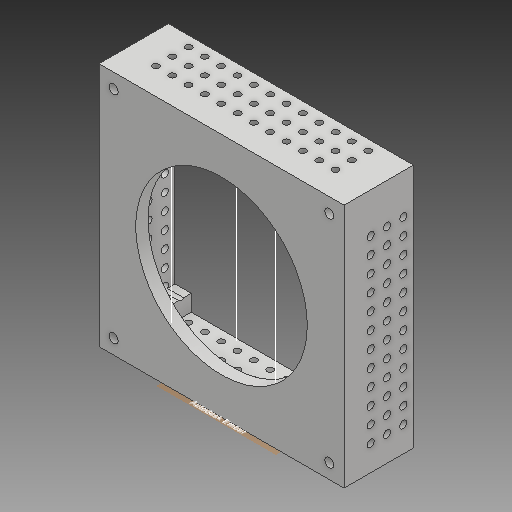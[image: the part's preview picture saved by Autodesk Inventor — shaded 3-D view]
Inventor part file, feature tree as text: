
AUTODESK INVENTOR PART (.ipt)
format: ipt  version: 2018 (Build 220112000, 112)  size: 508,416 bytes
history: native  units: mm
features: sketch x8, extrude x5, pattern_linear x2
ambient origin geometry x8: Origin, YZ Plane, XZ Plane, XY Plane, X Axis, Y Axis, Z Axis, Center Point
bodies: Solid1 (feature_tree)
feature tree (15):
  sketch  "Sketch1"  dims[d0=150.0mm d1=150.0mm]
  extrude  "Extrusion1"  Depth=150.0mm
  extrude  "Extrusion3"  Depth=4.0mm
  extrude  "Extrusion4"  Depth=10.0mm
  pattern_linear  "Rectangular Pattern1"  Count1=2 Spacing1=132.0mm
  extrude  "Extrusion5"  Depth=132.0mm
  pattern_linear  "Rectangular Pattern2"  Count1=8 Spacing1=0.0mm
  sketch  "Sketch9"  dims[d17=20.0mm d19=132.0mm d20=5.5mm d21=80.0mm d22=0.0mm]
  extrude  "Extrusion8"  Depth=132.0mm
  sketch  "Sketch11"  dims[d45=4.0mm d46=40.0mm d47=0.0mm]
  sketch  "Sketch2"  dims[d2=7.5mm d3=0.0mm d7=4.0mm]
  sketch  "Sketch4"  dims[d8=35.0mm d9=0.0mm d10=10.0mm]
  sketch  "Sketch5"  dims[d11=10.0mm]
  sketch  "Sketch6"  dims[d12=35.0mm d13=0.0mm d14=20.0mm d16=132.0mm]
  sketch  "Sketch10"  dims[d23=20.0mm d25=132.0mm d26=20.0mm d28=132.0mm]
